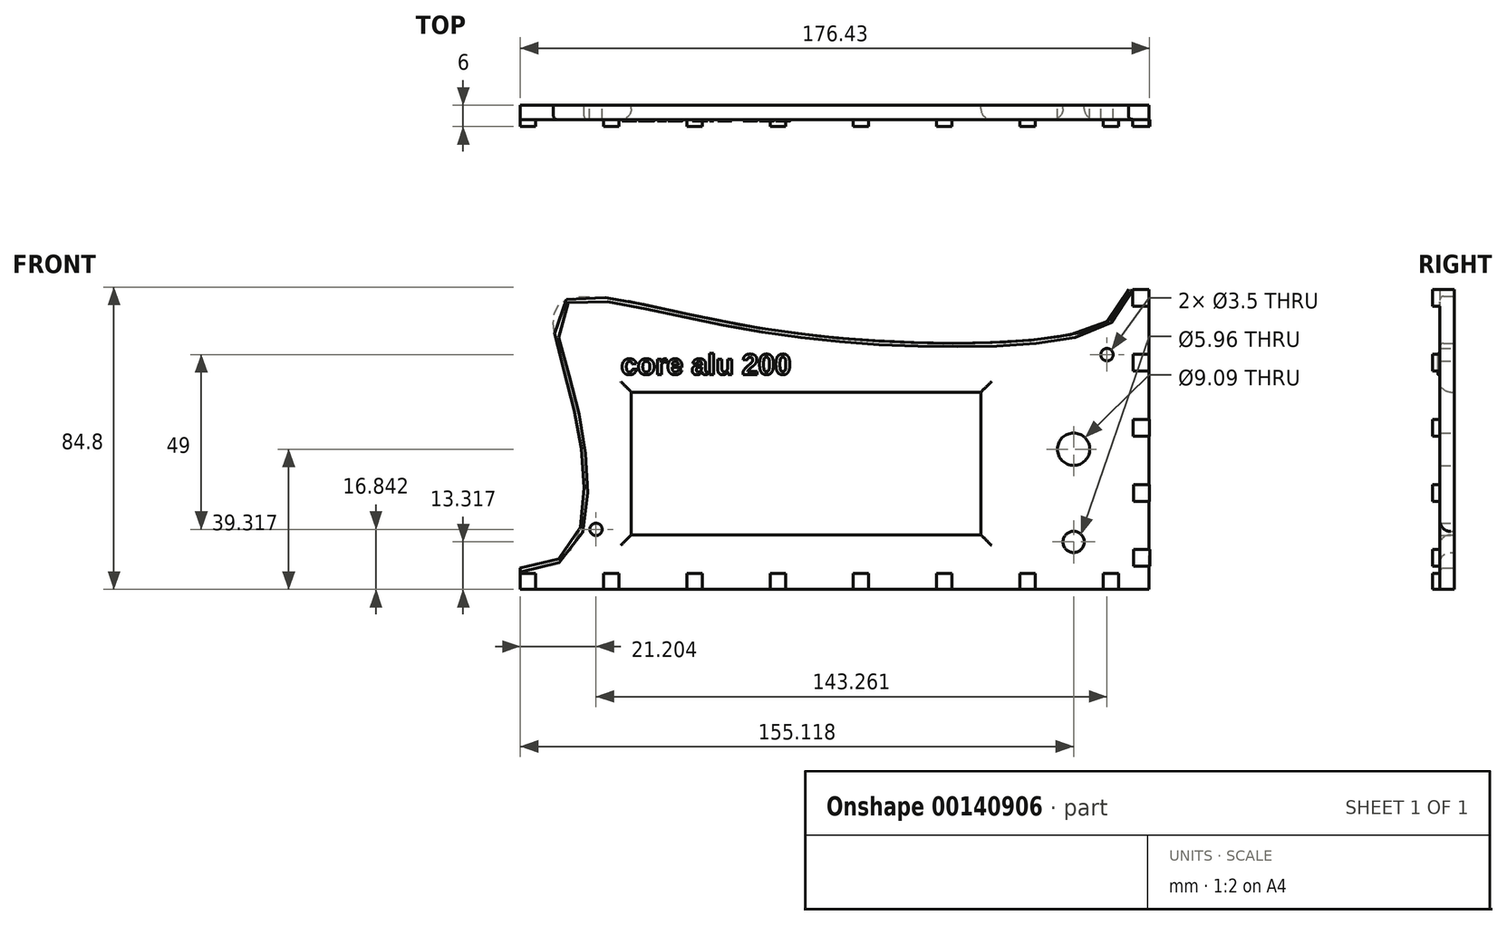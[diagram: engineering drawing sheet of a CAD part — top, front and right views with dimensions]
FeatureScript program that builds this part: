
annotation { "Feature Type Name" : "Feature", "Feature Type Description" : "" }
export const myFeature = defineFeature(function(context is Context, id is Id, definition is map)
    precondition{}
    {
        {
            var Q0;
            Q0=qCreatedBy(makeId("Front.planeOp"),FACE);
            var sketch = newSketch(context, id + "F0", { "sketchPlane" : qUnion([Q0])});
            skLineSegment(sketch, "E0.bottom", {"start": v(-77.31, 21.96) * mm, "end": v(72.69, 21.96) * mm, "construction": true});
            skLineSegment(sketch, "E0.top", {"start": v(-77.31, -41.04) * mm, "end": v(72.69, -41.04) * mm, "construction": true});
            skLineSegment(sketch, "E0.left", {"start": v(-77.31, 21.96) * mm, "end": v(-77.31, -41.04) * mm, "construction": true});
            skLineSegment(sketch, "E0.right", {"start": v(72.69, 21.96) * mm, "end": v(72.69, -41.04) * mm, "construction": true});
            skLineSegment(sketch, "E1", {"start": v(80.76, -46.36) * mm, "end": v(80.76, 37.8) * mm});
            skLineSegment(sketch, "E2", {"start": v(80.76, -46.36) * mm, "end": v(-95.43, -46.36) * mm});
            skLineSegment(sketch, "E3", {"start": v(-95.43, -46.36) * mm, "end": v(-95.43, -40.35) * mm});
            skLineSegment(sketch, "E4", {"start": v(80.76, 37.8) * mm, "end": v(75.04, 37.8) * mm});
            skFitSpline(sketch, "E5", {"points": [v(-95.43, -40.35) * mm, v(-82.26, -36.25) * mm, v(-78.93, -2.99) * mm, v(-85.2, 22.25) * mm, v(-85.4, 32.43) * mm, v(-78.74, 35.75) * mm, v(-51.35, 31.45) * mm, v(0, 23.62) * mm, v(62.52, 25.97) * mm, v(72.5, 32.43) * mm, v(75.04, 37.8) * mm, v(80.76, 37.8) * mm, v(80.76, -46.36) * mm, v(-95.43, -46.36) * mm, v(-95.43, -40.35) * mm]});
            skLineSegment(sketch, "E6.bottom", {"start": v(-64.31, 8.96) * mm, "end": v(33.69, 8.96) * mm});
            skLineSegment(sketch, "E6.top", {"start": v(-64.31, -31.04) * mm, "end": v(33.69, -31.04) * mm});
            skLineSegment(sketch, "E6.left", {"start": v(-64.31, 8.96) * mm, "end": v(-64.31, -31.04) * mm});
            skLineSegment(sketch, "E6.right", {"start": v(33.69, 8.96) * mm, "end": v(33.69, -31.04) * mm});
            skCircle(sketch, "E7", {"center": v(59.69, -7.04) * mm, "radius": 4.55 * mm});
            skCircle(sketch, "E8", {"center": v(59.69, -33.04) * mm, "radius": 2.98 * mm});
            skCircle(sketch, "E9", {"center": v(69.04, 19.48) * mm, "radius": 1.75 * mm});
            skCircle(sketch, "E10", {"center": v(69.63, -29.52) * mm, "radius": 1.75 * mm});
            skCircle(sketch, "E11", {"center": v(-74.23, -29.52) * mm, "radius": 1.75 * mm});
            skCircle(sketch, "E12", {"center": v(-74.96, 19.48) * mm, "radius": 1.75 * mm});
            skSolve(sketch);
        }
        {
            var Q0;
            Q0=makeQuery(id+"F0.imprint","IMPRINT",FACE,{"disambiguationData":[TD([[makeQuery(id+"F0.imprint","IMPRINT",EDGE,{"derivedFrom":sQuery(id+"F0.wireOp",EDGE,"E1")}),1.0]])]});
            var Q1;
            Q1=makeQuery(id+"F0.imprint","IMPRINT",FACE,{"disambiguationData":[TD([[makeQuery(id+"F0.imprint","IMPRINT",EDGE,{"derivedFrom":sQuery(id+"F0.wireOp",EDGE,"E10")}),1.0]])]});
            var Q2;
            Q2=makeQuery(id+"F0.imprint","IMPRINT",FACE,{"disambiguationData":[TD([[makeQuery(id+"F0.imprint","IMPRINT",EDGE,{"derivedFrom":sQuery(id+"F0.wireOp",EDGE,"E12")}),1.0]])]});
            extrude(context, id + "F1", {"entities" : qUnion([Q0, Q1, Q2]), "depth" : 4 * mm});
        }
        {
            var Q0;
            Q0=makeQuery(id+"F1.opExtrude","CAP_EDGE",EDGE,{"disambiguationData":[OSD([sQuery(id+"F0.wireOp",EDGE,"E5")])],"isStart":false});
            fillet(context, id + "F2", {"entities" : qUnion([Q0]), "radius" : 1 * mm, "tangentPropagation" : true, "allowEdgeOverflow" : false});
        }
        {
            var Q0;
            Q0=makeQuery(id+"F1.opExtrude","CAP_FACE",FACE,{"disambiguationData":[OSD([sQuery(id+"F0.wireOp",EDGE,"E1"),sQuery(id+"F0.wireOp",EDGE,"E2"),sQuery(id+"F0.wireOp",EDGE,"E3"),sQuery(id+"F0.wireOp",EDGE,"E4"),sQuery(id+"F0.wireOp",EDGE,"E5"),sQuery(id+"F0.wireOp",EDGE,"E6.bottom"),sQuery(id+"F0.wireOp",EDGE,"E6.top"),sQuery(id+"F0.wireOp",EDGE,"E6.left"),sQuery(id+"F0.wireOp",EDGE,"E6.right"),sQuery(id+"F0.wireOp",EDGE,"E7"),sQuery(id+"F0.wireOp",EDGE,"E8"),sQuery(id+"F0.wireOp",EDGE,"E9"),sQuery(id+"F0.wireOp",EDGE,"E11")])],"isStart":false});
            var sketch = newSketch(context, id + "F3", { "sketchPlane" : qUnion([Q0])});
            skLineSegment(sketch, "E13.bottom", {"start": v(-95.43, -46.36) * mm, "end": v(-91.12, -46.36) * mm});
            skLineSegment(sketch, "E13.top", {"start": v(-95.43, -41.86) * mm, "end": v(-91.12, -41.86) * mm});
            skLineSegment(sketch, "E13.left", {"start": v(-95.43, -46.36) * mm, "end": v(-95.43, -41.86) * mm});
            skLineSegment(sketch, "E13.right", {"start": v(-91.12, -46.36) * mm, "end": v(-91.12, -41.86) * mm});
            skLineSegment(sketch, "E14.1.0.0", {"start": v(-67.78, -46.36) * mm, "end": v(-67.78, -41.86) * mm});
            skLineSegment(sketch, "E14.1.0.1", {"start": v(-72.09, -46.36) * mm, "end": v(-72.09, -41.86) * mm});
            skLineSegment(sketch, "E14.1.0.2", {"start": v(-72.09, -41.86) * mm, "end": v(-67.78, -41.86) * mm});
            skLineSegment(sketch, "E14.1.0.3", {"start": v(-72.09, -46.36) * mm, "end": v(-67.78, -46.36) * mm});
            skLineSegment(sketch, "E14.2.0.0", {"start": v(-44.44, -46.36) * mm, "end": v(-44.44, -41.86) * mm});
            skLineSegment(sketch, "E14.2.0.1", {"start": v(-48.74, -46.36) * mm, "end": v(-48.74, -41.86) * mm});
            skLineSegment(sketch, "E14.2.0.2", {"start": v(-48.74, -41.86) * mm, "end": v(-44.44, -41.86) * mm});
            skLineSegment(sketch, "E14.2.0.3", {"start": v(-48.74, -46.36) * mm, "end": v(-44.44, -46.36) * mm});
            skLineSegment(sketch, "E14.3.0.0", {"start": v(-21.1, -46.36) * mm, "end": v(-21.1, -41.86) * mm});
            skLineSegment(sketch, "E14.3.0.1", {"start": v(-25.4, -46.36) * mm, "end": v(-25.4, -41.86) * mm});
            skLineSegment(sketch, "E14.3.0.2", {"start": v(-25.4, -41.86) * mm, "end": v(-21.1, -41.86) * mm});
            skLineSegment(sketch, "E14.3.0.3", {"start": v(-25.4, -46.36) * mm, "end": v(-21.1, -46.36) * mm});
            skLineSegment(sketch, "E14.4.0.0", {"start": v(2.24, -46.36) * mm, "end": v(2.24, -41.86) * mm});
            skLineSegment(sketch, "E14.4.0.1", {"start": v(-2.06, -46.36) * mm, "end": v(-2.06, -41.86) * mm});
            skLineSegment(sketch, "E14.4.0.2", {"start": v(-2.06, -41.86) * mm, "end": v(2.24, -41.86) * mm});
            skLineSegment(sketch, "E14.4.0.3", {"start": v(-2.06, -46.36) * mm, "end": v(2.24, -46.36) * mm});
            skLineSegment(sketch, "E14.5.0.0", {"start": v(25.59, -46.36) * mm, "end": v(25.59, -41.86) * mm});
            skLineSegment(sketch, "E14.5.0.1", {"start": v(21.28, -46.36) * mm, "end": v(21.28, -41.86) * mm});
            skLineSegment(sketch, "E14.5.0.2", {"start": v(21.28, -41.86) * mm, "end": v(25.59, -41.86) * mm});
            skLineSegment(sketch, "E14.5.0.3", {"start": v(21.28, -46.36) * mm, "end": v(25.59, -46.36) * mm});
            skLineSegment(sketch, "E14.6.0.0", {"start": v(48.93, -46.36) * mm, "end": v(48.93, -41.86) * mm});
            skLineSegment(sketch, "E14.6.0.1", {"start": v(44.62, -46.36) * mm, "end": v(44.62, -41.86) * mm});
            skLineSegment(sketch, "E14.6.0.2", {"start": v(44.62, -41.86) * mm, "end": v(48.93, -41.86) * mm});
            skLineSegment(sketch, "E14.6.0.3", {"start": v(44.62, -46.36) * mm, "end": v(48.93, -46.36) * mm});
            skLineSegment(sketch, "E14.7.0.0", {"start": v(72.27, -46.36) * mm, "end": v(72.27, -41.86) * mm});
            skLineSegment(sketch, "E14.7.0.1", {"start": v(67.97, -46.36) * mm, "end": v(67.97, -41.86) * mm});
            skLineSegment(sketch, "E14.7.0.2", {"start": v(67.97, -41.86) * mm, "end": v(72.27, -41.86) * mm});
            skLineSegment(sketch, "E14.7.0.3", {"start": v(67.97, -46.36) * mm, "end": v(72.27, -46.36) * mm});
            skLineSegment(sketch, "E14.direction1", {"start": v(-95.43, -46.36) * mm, "end": v(-72.09, -46.36) * mm, "construction": true});
            skLineSegment(sketch, "E15.bottom", {"start": v(80.76, 37.8) * mm, "end": v(76.26, 37.8) * mm});
            skLineSegment(sketch, "E15.top", {"start": v(80.76, 33.08) * mm, "end": v(76.26, 33.08) * mm});
            skLineSegment(sketch, "E15.left", {"start": v(80.76, 37.8) * mm, "end": v(80.76, 33.08) * mm});
            skLineSegment(sketch, "E15.right", {"start": v(76.26, 37.8) * mm, "end": v(76.26, 33.08) * mm});
            skLineSegment(sketch, "E16.1.0.0", {"start": v(80.82, 19.56) * mm, "end": v(80.82, 14.84) * mm});
            skLineSegment(sketch, "E16.1.0.1", {"start": v(80.82, 14.84) * mm, "end": v(76.32, 14.84) * mm});
            skLineSegment(sketch, "E16.1.0.2", {"start": v(80.82, 19.56) * mm, "end": v(76.32, 19.56) * mm});
            skLineSegment(sketch, "E16.1.0.3", {"start": v(76.32, 19.56) * mm, "end": v(76.32, 14.84) * mm});
            skLineSegment(sketch, "E16.2.0.0", {"start": v(80.88, 1.32) * mm, "end": v(80.88, -3.4) * mm});
            skLineSegment(sketch, "E16.2.0.1", {"start": v(80.88, -3.4) * mm, "end": v(76.38, -3.4) * mm});
            skLineSegment(sketch, "E16.2.0.2", {"start": v(80.88, 1.32) * mm, "end": v(76.38, 1.32) * mm});
            skLineSegment(sketch, "E16.2.0.3", {"start": v(76.38, 1.32) * mm, "end": v(76.38, -3.4) * mm});
            skLineSegment(sketch, "E16.3.0.0", {"start": v(80.94, -16.92) * mm, "end": v(80.94, -21.64) * mm});
            skLineSegment(sketch, "E16.3.0.1", {"start": v(80.94, -21.64) * mm, "end": v(76.44, -21.64) * mm});
            skLineSegment(sketch, "E16.3.0.2", {"start": v(80.94, -16.92) * mm, "end": v(76.44, -16.92) * mm});
            skLineSegment(sketch, "E16.3.0.3", {"start": v(76.44, -16.92) * mm, "end": v(76.44, -21.64) * mm});
            skLineSegment(sketch, "E16.4.0.0", {"start": v(81, -35.16) * mm, "end": v(81, -39.88) * mm});
            skLineSegment(sketch, "E16.4.0.1", {"start": v(81, -39.88) * mm, "end": v(76.5, -39.88) * mm});
            skLineSegment(sketch, "E16.4.0.2", {"start": v(81, -35.16) * mm, "end": v(76.5, -35.16) * mm});
            skLineSegment(sketch, "E16.4.0.3", {"start": v(76.5, -35.16) * mm, "end": v(76.5, -39.88) * mm});
            skLineSegment(sketch, "E16.direction1", {"start": v(76.26, 33.08) * mm, "end": v(76.32, 14.84) * mm, "construction": true});
            skSolve(sketch);
        }
        {
            var Q0;
            Q0=qSketchRegion(id+"F3",true);
            extrude(context, id + "F4", {"entities" : qUnion([Q0]), "operationType" : NewBodyOperationType.ADD, "depth" : 2 * mm});
        }
        {
            var Q0;
            Q0=makeQuery(id+"F1.opExtrude","CAP_EDGE",EDGE,{"disambiguationData":[OSD([sQuery(id+"F0.wireOp",EDGE,"E6.bottom")])],"isStart":false});
            var Q1;
            Q1=makeQuery(id+"F1.opExtrude","CAP_EDGE",EDGE,{"disambiguationData":[OSD([sQuery(id+"F0.wireOp",EDGE,"E6.right")])],"isStart":false});
            var Q2;
            Q2=makeQuery(id+"F1.opExtrude","CAP_EDGE",EDGE,{"disambiguationData":[OSD([sQuery(id+"F0.wireOp",EDGE,"E6.top")])],"isStart":false});
            var Q3;
            Q3=makeQuery(id+"F1.opExtrude","CAP_EDGE",EDGE,{"disambiguationData":[OSD([sQuery(id+"F0.wireOp",EDGE,"E6.left")])],"isStart":false});
            fillet(context, id + "F5", {"entities" : qUnion([Q0, Q1, Q2, Q3]), "radius" : 3 * mm, "tangentPropagation" : true, "allowEdgeOverflow" : false});
        }
        {
            var Q0;
            Q0=makeQuery(id+"F1.opExtrude","CAP_EDGE",EDGE,{"disambiguationData":[OSD([sQuery(id+"F0.wireOp",EDGE,"E8")])],"isStart":false});
            fillet(context, id + "F6", {"entities" : qUnion([Q0]), "radius" : 3 * mm, "tangentPropagation" : true, "allowEdgeOverflow" : false});
        }
        {
            var Q0;
            Q0=makeQuery(id+"F1.opExtrude","CAP_FACE",FACE,{"disambiguationData":[OSD([sQuery(id+"F0.wireOp",EDGE,"E1"),sQuery(id+"F0.wireOp",EDGE,"E2"),sQuery(id+"F0.wireOp",EDGE,"E3"),sQuery(id+"F0.wireOp",EDGE,"E4"),sQuery(id+"F0.wireOp",EDGE,"E5"),sQuery(id+"F0.wireOp",EDGE,"E6.bottom"),sQuery(id+"F0.wireOp",EDGE,"E6.top"),sQuery(id+"F0.wireOp",EDGE,"E6.left"),sQuery(id+"F0.wireOp",EDGE,"E6.right"),sQuery(id+"F0.wireOp",EDGE,"E7"),sQuery(id+"F0.wireOp",EDGE,"E8"),sQuery(id+"F0.wireOp",EDGE,"E9"),sQuery(id+"F0.wireOp",EDGE,"E11")])],"isStart":false});
            var sketch = newSketch(context, id + "F7", { "sketchPlane" : qUnion([Q0])});
            skText(sketch, "E17", { "text": "core alu 200", "fontName": "Arimo-Bold.ttf"});
            const initialGuessF7  = {"E17": [-0.06722, 0.0139, 1, 0, 0.00594]};
            skSetInitialGuess(sketch, initialGuessF7);
            skSolve(sketch);
        }
        {
            var Q0;
            Q0=qSketchRegion(id+"F7",true);
            extrude(context, id + "F8", {"entities" : qUnion([Q0]), "operationType" : NewBodyOperationType.ADD, "depth" : 0.5 * mm});
        }
    });
